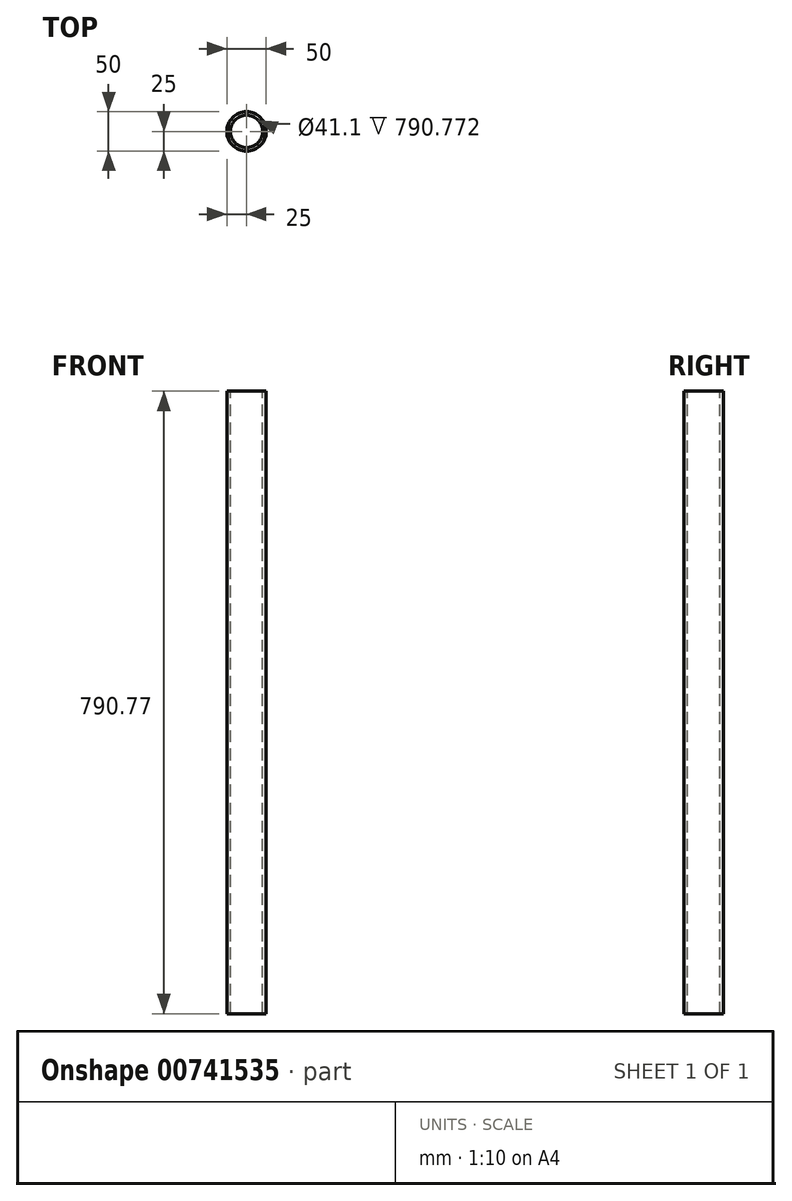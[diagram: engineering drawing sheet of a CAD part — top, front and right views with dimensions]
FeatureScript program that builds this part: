
annotation { "Feature Type Name" : "Feature", "Feature Type Description" : "" }
export const myFeature = defineFeature(function(context is Context, id is Id, definition is map)
    precondition{}
    {
        {
            var Q0;
            Q0=qCreatedBy(makeId("Front.planeOp"),FACE);
            var sketch = newSketch(context, id + "F0", { "sketchPlane" : qUnion([Q0])});
            skLineSegment(sketch, "E0", {"start": v(0, 0) * mm, "end": v(25, 0) * mm});
            skLineSegment(sketch, "E1", {"start": v(25, 0) * mm, "end": v(25, 850) * mm});
            skLineSegment(sketch, "E2", {"start": v(25, 850) * mm, "end": v(0, 850) * mm});
            skLineSegment(sketch, "E3", {"start": v(0, 850) * mm, "end": v(0, 0) * mm});
            skLineSegment(sketch, "E4", {"start": v(0, 790.77) * mm, "end": v(25, 790.77) * mm});
            skLineSegment(sketch, "E5", {"start": v(20.55, 0) * mm, "end": v(20.55, 850) * mm});
            skSolve(sketch);
        }
        {
            var Q0;
            {var subQ0=sQuery(id+"F0.wireOp",EDGE,"E1");var subQ1=sQuery(id+"F0.wireOp",EDGE,"E0");var subQ2=makeQuery(id+"F0.imprint","INTERSECT",VERTEX,{"derivedFrom":[subQ1,subQ0]});Q0=makeQuery(id+"F0.imprint","IMPRINT",FACE,{"disambiguationData":[TD([[makeQuery(id+"F0.imprint","IMPRINT",EDGE,{"disambiguationData":[TD([[subQ2,1.0]])],"derivedFrom":subQ1}),1.0]])]});}
            var Q1;
            Q1=sQuery(id+"F0.wireOp",EDGE,"E3");
            revolve(context, id + "F1", {"surfaceOperationType" : NewSurfaceOperationType.NEW, "entities" : qUnion([Q0]), "axis" : qUnion([Q1]), "revolveType" : RevolveType.FULL});
        }
    });
